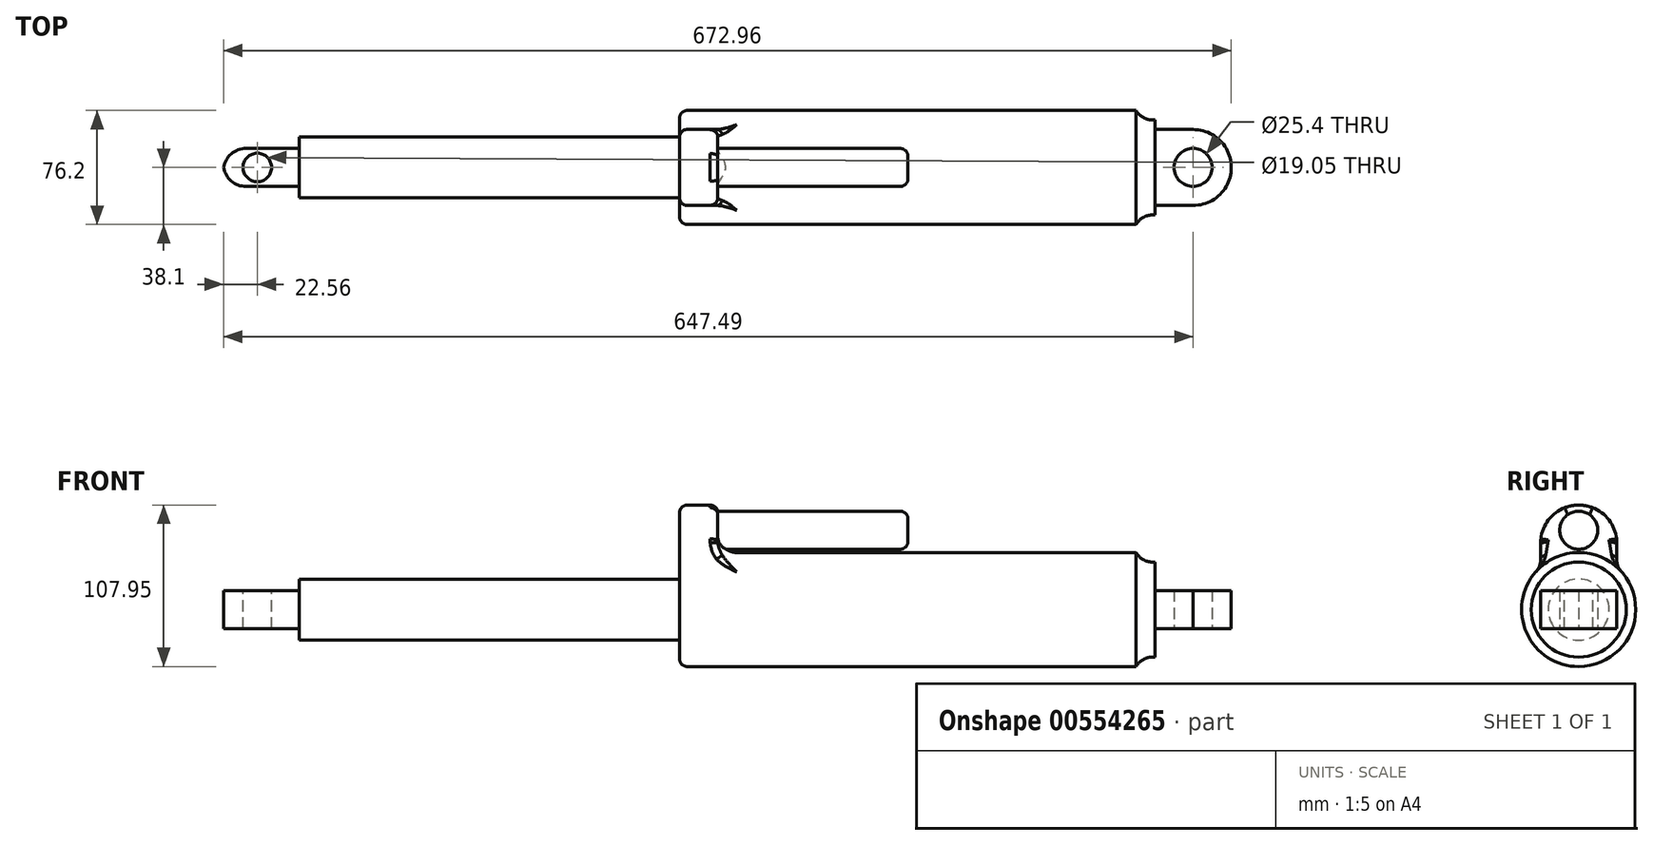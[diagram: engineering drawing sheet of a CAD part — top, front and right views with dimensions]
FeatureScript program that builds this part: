
annotation { "Feature Type Name" : "Feature", "Feature Type Description" : "" }
export const myFeature = defineFeature(function(context is Context, id is Id, definition is map)
    precondition{}
    {
        {
            var Q0;
            Q0=qCreatedBy(makeId("Right.planeOp"),FACE);
            var sketch = newSketch(context, id + "F0", { "sketchPlane" : qUnion([Q0])});
            skCircle(sketch, "E0", {"center": v(0, 0) * mm, "radius": 38.1 * mm});
            skSolve(sketch);
        }
        {
            var Q0;
            Q0=sQuery(id+"F0.wireOp",EDGE,"E0");
            extrude(context, id + "F1", {"bodyType" : ToolBodyType.SURFACE, "surfaceEntities" : qUnion([Q0]), "depth" : 304.8 * mm, "offsetDistance" : 25.4 * mm});
        }
        {
            var Q0;
            Q0=qCreatedBy(makeId("Right.planeOp"),FACE);
            var sketch = newSketch(context, id + "F2", { "sketchPlane" : qUnion([Q0])});
            skCircle(sketch, "E1", {"center": v(0, 0) * mm, "radius": 20.37 * mm});
            skSolve(sketch);
        }
        {
            var Q0;
            Q0=sQuery(id+"F2.wireOp",EDGE,"E1");
            extrude(context, id + "F3", {"bodyType" : ToolBodyType.SURFACE, "surfaceEntities" : qUnion([Q0]), "oppositeDirection" : true, "depth" : 254 * mm, "offsetDistance" : 25.4 * mm});
        }
        {
            var Q0;
            Q0=qCreatedBy(makeId("Right.planeOp"),FACE);
            var sketch = newSketch(context, id + "F4", { "sketchPlane" : qUnion([Q0])});
            skLineSegment(sketch, "E2.bottom", {"start": v(0, 0) * mm, "end": v(25.4, 0) * mm});
            skLineSegment(sketch, "E2.top", {"start": v(0, 69.85) * mm, "end": v(25.4, 69.85) * mm});
            skLineSegment(sketch, "E2.left", {"start": v(0, 0) * mm, "end": v(0, 69.85) * mm});
            skLineSegment(sketch, "E2.right", {"start": v(25.4, 0) * mm, "end": v(25.4, 69.85) * mm});
            skLineSegment(sketch, "E3.bottom", {"start": v(0, 0) * mm, "end": v(-25.4, 0) * mm});
            skLineSegment(sketch, "E3.top", {"start": v(0, 69.85) * mm, "end": v(-25.4, 69.85) * mm});
            skLineSegment(sketch, "E3.right", {"start": v(-25.4, 0) * mm, "end": v(-25.4, 69.85) * mm});
            skSolve(sketch);
        }
        {
            var Q0;
            Q0=makeQuery(id+"F4.imprint","IMPRINT",FACE,{"disambiguationData":[TD([[makeQuery(id+"F4.imprint","IMPRINT",EDGE,{"derivedFrom":sQuery(id+"F4.wireOp",EDGE,"E3.bottom")}),-1.0]])]});
            var Q1;
            Q1=makeQuery(id+"F4.imprint","IMPRINT",FACE,{"disambiguationData":[TD([[makeQuery(id+"F4.imprint","IMPRINT",EDGE,{"derivedFrom":sQuery(id+"F4.wireOp",EDGE,"E2.bottom")}),1.0]])]});
            extrude(context, id + "F5", {"entities" : qUnion([Q0, Q1]), "depth" : 25.4 * mm, "offsetDistance" : 25.4 * mm});
        }
        {
            var Q0;
            Q0=makeQuery(id+"F5.opExtrude","CAP_FACE",FACE,{"disambiguationData":[OSD([sQuery(id+"F4.wireOp",EDGE,"E2.bottom"),sQuery(id+"F4.wireOp",EDGE,"E2.top"),sQuery(id+"F4.wireOp",EDGE,"E2.right"),sQuery(id+"F4.wireOp",EDGE,"E3.bottom"),sQuery(id+"F4.wireOp",EDGE,"E3.top"),sQuery(id+"F4.wireOp",EDGE,"E3.right")])],"isStart":false});
            var sketch = newSketch(context, id + "F6", { "sketchPlane" : qUnion([Q0])});
            skPoint(sketch, "E4", {"position": v(0, 53.06) * mm});
            skCircle(sketch, "E5", {"center": v(0, 53.06) * mm, "radius": 12.7 * mm});
            skSolve(sketch);
        }
        {
            var Q0;
            {var subQ0=sQuery(id+"F6.wireOp",EDGE,"E5");var subQ1=makeQuery(id+"F5.opExtrude","CAP_EDGE",EDGE,{"disambiguationData":[OSD([sQuery(id+"F4.wireOp",EDGE,"E2.top"),sQuery(id+"F4.wireOp",EDGE,"E3.top")])],"isStart":false});var subQ2=makeQuery(id+"F6.imprint","INTERSECT",VERTEX,{"disambiguationData":[OD(0.0)],"derivedFrom":[subQ1,subQ0]});Q0=makeQuery(id+"F6.imprint","IMPRINT",FACE,{"disambiguationData":[TD([[makeQuery(id+"F6.imprint","IMPRINT",EDGE,{"disambiguationData":[TD([[subQ2,1.0]])],"derivedFrom":subQ0}),1.0]])]});}
            extrude(context, id + "F7", {"entities" : qUnion([Q0]), "operationType" : NewBodyOperationType.ADD, "depth" : 127 * mm, "offsetDistance" : 25.4 * mm});
        }
        {
            var Q0;
            Q0=qCreatedBy(makeId("Right.planeOp"),FACE);
            var sketch = newSketch(context, id + "F8", { "sketchPlane" : qUnion([Q0])});
            skLineSegment(sketch, "E6.bottom", {"start": v(25.4, -12.7) * mm, "end": v(-25.4, -12.7) * mm});
            skLineSegment(sketch, "E6.top", {"start": v(25.4, 12.7) * mm, "end": v(-25.4, 12.7) * mm});
            skLineSegment(sketch, "E6.left", {"start": v(25.4, -12.7) * mm, "end": v(25.4, 12.7) * mm});
            skLineSegment(sketch, "E6.right", {"start": v(-25.4, -12.7) * mm, "end": v(-25.4, 12.7) * mm});
            skPoint(sketch, "E6.middle", {"position": v(0, 0) * mm});
            skSolve(sketch);
        }
        {
            var Q0;
            Q0=makeQuery(id+"F8.imprint","IMPRINT",FACE,{"disambiguationData":[TD([[makeQuery(id+"F8.imprint","IMPRINT",EDGE,{"derivedFrom":sQuery(id+"F8.wireOp",EDGE,"E6.bottom")}),-1.0]])]});
            extrude(context, id + "F9", {"entities" : qUnion([Q0]), "operationType" : NewBodyOperationType.ADD, "depth" : 342.9 * mm, "offsetDistance" : 25.4 * mm});
        }
        {
            var Q0;
            Q0=qCreatedBy(makeId("Top.planeOp"),FACE);
            var sketch = newSketch(context, id + "F10", { "sketchPlane" : qUnion([Q0])});
            skPoint(sketch, "E7", {"position": v(343.01, 0) * mm});
            skCircle(sketch, "E8", {"center": v(343.01, 0) * mm, "radius": 25.36 * mm});
            skSolve(sketch);
        }
        {
            var Q0;
            Q0=makeQuery(id+"F10.imprint","IMPRINT",FACE,{"disambiguationData":[TD([[makeQuery(id+"F10.imprint","IMPRINT",EDGE,{"derivedFrom":sQuery(id+"F10.wireOp",EDGE,"E8")}),1.0]])]});
            extrude(context, id + "F11", {"entities" : qUnion([Q0]), "operationType" : NewBodyOperationType.ADD, "depth" : 12.7 * mm, "offsetDistance" : 25.4 * mm});
        }
        {
            var Q0;
            Q0=makeQuery(id+"F11.opExtrude","CAP_FACE",FACE,{"disambiguationData":[OSD([sQuery(id+"F10.wireOp",EDGE,"E8")])],"isStart":true});
            extrude(context, id + "F12", {"entities" : qUnion([Q0]), "operationType" : NewBodyOperationType.ADD, "depth" : 12.7 * mm, "offsetDistance" : 25.4 * mm});
        }
        {
            var Q0;
            Q0=makeQuery(id+"F12.boolean.opBoolean","MERGE",FACE,{"derivedFrom":[makeQuery(id+"F9.opExtrude","SWEPT_FACE",FACE,{"disambiguationData":[OSD([sQuery(id+"F8.wireOp",EDGE,"E6.bottom")])]}),makeQuery(id+"F12.opExtrude","CAP_FACE",FACE,{"disambiguationData":[OSD([sQuery(id+"F10.wireOp",EDGE,"E8")])],"isStart":false})]});
            var sketch = newSketch(context, id + "F13", { "sketchPlane" : qUnion([Q0])});
            skPoint(sketch, "E9", {"position": v(342.9, 0) * mm});
            skSolve(sketch);
        }
        {
            var Q0;
            Q0=sQuery(id+"F13.wireOp",VERTEX,"E9");
            var Q1;
            Q1=makeQuery(id+"F5.opExtrude","SWEPT_BODY",BODY,{"disambiguationData":[OSD([sQuery(id+"F4.wireOp",EDGE,"E2.bottom"),sQuery(id+"F4.wireOp",EDGE,"E2.top"),sQuery(id+"F4.wireOp",EDGE,"E2.right"),sQuery(id+"F4.wireOp",EDGE,"E3.bottom"),sQuery(id+"F4.wireOp",EDGE,"E3.top"),sQuery(id+"F4.wireOp",EDGE,"E3.right")])]});
            hole(context, id + "F14", {"style" : HoleStyle.SIMPLE, "endStyle" : HoleEndStyle.THROUGH, "holeDiameter" : 25.4 * mm, "isTappedThrough" : true, "tappedDepth" : 12.7 * mm, "tapClearance" : 3, "locations" : qUnion([Q0]), "scope" : qUnion([Q1])});
        }
        {
            var Q0;
            Q0=qCreatedBy(makeId("Right.planeOp"),FACE);
            var sketch = newSketch(context, id + "F15", { "sketchPlane" : qUnion([Q0])});
            skLineSegment(sketch, "E10.bottom", {"start": v(7.2, -12.7) * mm, "end": v(-7.2, -12.7) * mm});
            skLineSegment(sketch, "E10.top", {"start": v(7.2, 12.7) * mm, "end": v(-7.2, 12.7) * mm});
            skLineSegment(sketch, "E10.left", {"start": v(7.2, -12.7) * mm, "end": v(7.2, 12.7) * mm});
            skLineSegment(sketch, "E10.right", {"start": v(-7.2, -12.7) * mm, "end": v(-7.2, 12.7) * mm});
            skPoint(sketch, "E10.middle", {"position": v(0, 0) * mm});
            skSolve(sketch);
        }
        {
            var Q0;
            Q0=makeQuery(id+"F15.imprint","IMPRINT",FACE,{"disambiguationData":[TD([[makeQuery(id+"F15.imprint","IMPRINT",EDGE,{"derivedFrom":sQuery(id+"F15.wireOp",EDGE,"E10.bottom")}),-1.0]])]});
            extrude(context, id + "F16", {"entities" : qUnion([Q0]), "operationType" : NewBodyOperationType.ADD, "depth" : 25.4 * mm, "offsetDistance" : 25.4 * mm});
        }
        {
            var Q0;
            Q0=qCreatedBy(makeId("Right.planeOp"),FACE);
            var sketch = newSketch(context, id + "F17", { "sketchPlane" : qUnion([Q0])});
            skLineSegment(sketch, "E11.bottom", {"start": v(-12.7, -12.7) * mm, "end": v(12.7, -12.7) * mm});
            skLineSegment(sketch, "E11.top", {"start": v(-12.7, 12.7) * mm, "end": v(12.7, 12.7) * mm});
            skLineSegment(sketch, "E11.left", {"start": v(-12.7, -12.7) * mm, "end": v(-12.7, 12.7) * mm});
            skLineSegment(sketch, "E11.right", {"start": v(12.7, -12.7) * mm, "end": v(12.7, 12.7) * mm});
            skPoint(sketch, "E11.middle", {"position": v(0, 0) * mm});
            skSolve(sketch);
        }
        {
            var Q0;
            Q0=makeQuery(id+"F17.imprint","IMPRINT",FACE,{"disambiguationData":[TD([[makeQuery(id+"F17.imprint","IMPRINT",EDGE,{"derivedFrom":sQuery(id+"F17.wireOp",EDGE,"E11.bottom")}),1.0]])]});
            extrude(context, id + "F18", {"entities" : qUnion([Q0]), "operationType" : NewBodyOperationType.ADD, "oppositeDirection" : true, "depth" : 304.8 * mm, "offsetDistance" : 25.4 * mm});
        }
        {
            var Q0;
            Q0=makeQuery(id+"F18.opExtrude","CAP_EDGE",EDGE,{"disambiguationData":[OSD([sQuery(id+"F17.wireOp",EDGE,"E11.right")])],"isStart":false});
            var Q1;
            Q1=makeQuery(id+"F18.opExtrude","CAP_EDGE",EDGE,{"disambiguationData":[OSD([sQuery(id+"F17.wireOp",EDGE,"E11.left")])],"isStart":false});
            fillet(context, id + "F19", {"entities" : qUnion([Q0, Q1]), "radius" : 15.24 * mm, "tangentPropagation" : true, "allowEdgeOverflow" : false});
        }
        {
            var Q0;
            Q0=makeQuery(id+"F18.opExtrude","SWEPT_FACE",FACE,{"disambiguationData":[OSD([sQuery(id+"F17.wireOp",EDGE,"E11.top")])]});
            var sketch = newSketch(context, id + "F20", { "sketchPlane" : qUnion([Q0])});
            skPoint(sketch, "E12", {"position": v(-282.03, 0) * mm});
            skSolve(sketch);
        }
        {
            var Q0;
            Q0=sQuery(id+"F20.wireOp",VERTEX,"E12");
            var Q1;
            Q1=makeQuery(id+"F5.opExtrude","SWEPT_BODY",BODY,{"disambiguationData":[OSD([sQuery(id+"F4.wireOp",EDGE,"E2.bottom"),sQuery(id+"F4.wireOp",EDGE,"E2.top"),sQuery(id+"F4.wireOp",EDGE,"E2.right"),sQuery(id+"F4.wireOp",EDGE,"E3.bottom"),sQuery(id+"F4.wireOp",EDGE,"E3.top"),sQuery(id+"F4.wireOp",EDGE,"E3.right")])]});
            hole(context, id + "F21", {"style" : HoleStyle.SIMPLE, "endStyle" : HoleEndStyle.THROUGH, "holeDiameter" : 19.05 * mm, "isTappedThrough" : true, "tappedDepth" : 12.7 * mm, "tapClearance" : 3, "locations" : qUnion([Q0]), "scope" : qUnion([Q1])});
        }
        {
            var Q0;
            Q0=makeQuery(id+"F5.opExtrude","SWEPT_EDGE",EDGE,{"disambiguationData":[OSD([sQuery(id+"F4.wireOp",EDGE,"E3.top"),sQuery(id+"F4.wireOp",EDGE,"E3.right")])]});
            var Q1;
            Q1=makeQuery(id+"F5.opExtrude","SWEPT_EDGE",EDGE,{"disambiguationData":[OSD([sQuery(id+"F4.wireOp",EDGE,"E2.top"),sQuery(id+"F4.wireOp",EDGE,"E2.right")])]});
            fillet(context, id + "F22", {"entities" : qUnion([Q0, Q1]), "radius" : 25.4 * mm, "tangentPropagation" : true, "allowEdgeOverflow" : false});
        }
        {
            var Q0;
            Q0=makeQuery(id+"F7.opExtrude","CAP_EDGE",EDGE,{"disambiguationData":[OSD([sQuery(id+"F6.wireOp",EDGE,"E5")])],"isStart":false});
            fillet(context, id + "F23", {"entities" : qUnion([Q0]), "radius" : 5.08 * mm, "tangentPropagation" : true, "allowEdgeOverflow" : false});
        }
        {
            var Q0;
            Q0=qCreatedBy(makeId("Right.planeOp"),FACE);
            var sketch = newSketch(context, id + "F24", { "sketchPlane" : qUnion([Q0])});
            skCircle(sketch, "E13", {"center": v(0, 0) * mm, "radius": 31.75 * mm});
            skSolve(sketch);
        }
        {
            var Q0;
            Q0=sQuery(id+"F24.wireOp",EDGE,"E13");
            extrude(context, id + "F25", {"bodyType" : ToolBodyType.SURFACE, "surfaceEntities" : qUnion([Q0]), "depth" : 317.5 * mm, "offsetDistance" : 25.4 * mm});
        }
        {
            var Q0;
            Q0 = qSketchRegion(id + "F0", true);
            extrude(context, id + "F26", {"entities" : qUnion([Q0]), "operationType" : NewBodyOperationType.ADD, "depth" : 304.8 * mm, "offsetDistance" : 25.4 * mm});
        }
        {
            var Q0;
            Q0 = qSketchRegion(id + "F24", true);
            extrude(context, id + "F27", {"entities" : qUnion([Q0]), "operationType" : NewBodyOperationType.ADD, "depth" : 317.5 * mm, "offsetDistance" : 25.4 * mm});
        }
        {
            var Q0;
            Q0 = qSketchRegion(id + "F2", true);
            extrude(context, id + "F28", {"entities" : qUnion([Q0]), "operationType" : NewBodyOperationType.ADD, "oppositeDirection" : true, "depth" : 254 * mm, "offsetDistance" : 25.4 * mm});
        }
        {
            var Q0;
            Q0=makeQuery(id+"F27.boolean.opBoolean","INTERSECT",EDGE,{"derivedFrom":[makeQuery(id+"F26.opExtrude","CAP_FACE",FACE,{"disambiguationData":[OSD([sQuery(id+"F0.wireOp",EDGE,"E0")])],"isStart":false}),makeQuery(id+"F27.opExtrude","SWEPT_FACE",FACE,{"disambiguationData":[OSD([sQuery(id+"F24.wireOp",EDGE,"E13")])]})]});
            fillet(context, id + "F29", {"entities" : qUnion([Q0]), "radius" : 12.7 * mm, "tangentPropagation" : true, "allowEdgeOverflow" : false});
        }
        {
            var Q0;
            Q0=makeQuery(id+"F26.boolean.opBoolean","INTERSECT",EDGE,{"derivedFrom":[makeQuery(id+"F5.opExtrude","CAP_FACE",FACE,{"disambiguationData":[OSD([sQuery(id+"F4.wireOp",EDGE,"E2.bottom"),sQuery(id+"F4.wireOp",EDGE,"E2.top"),sQuery(id+"F4.wireOp",EDGE,"E2.right"),sQuery(id+"F4.wireOp",EDGE,"E3.bottom"),sQuery(id+"F4.wireOp",EDGE,"E3.top"),sQuery(id+"F4.wireOp",EDGE,"E3.right")])],"isStart":false}),makeQuery(id+"F26.opExtrude","SWEPT_FACE",FACE,{"disambiguationData":[OSD([sQuery(id+"F0.wireOp",EDGE,"E0")])]})]});
            fillet(context, id + "F30", {"entities" : qUnion([Q0]), "radius" : 12.7 * mm, "tangentPropagation" : true, "allowEdgeOverflow" : false});
        }
        {
            var Q0;
            Q0=makeQuery(id+"F26.boolean.opBoolean","INTERSECT",EDGE,{"derivedFrom":[makeQuery(id+"F9.boolean.opBoolean","MERGE",FACE,{"derivedFrom":[makeQuery(id+"F5.opExtrude","SWEPT_FACE",FACE,{"disambiguationData":[OSD([sQuery(id+"F4.wireOp",EDGE,"E3.right")])]}),makeQuery(id+"F9.opExtrude","SWEPT_FACE",FACE,{"disambiguationData":[OSD([sQuery(id+"F8.wireOp",EDGE,"E6.right")])]})]}),makeQuery(id+"F26.opExtrude","SWEPT_FACE",FACE,{"disambiguationData":[OSD([sQuery(id+"F0.wireOp",EDGE,"E0")])]})]});
            var Q1;
            Q1=makeQuery(id+"F26.boolean.opBoolean","INTERSECT",EDGE,{"derivedFrom":[makeQuery(id+"F9.boolean.opBoolean","MERGE",FACE,{"derivedFrom":[makeQuery(id+"F5.opExtrude","SWEPT_FACE",FACE,{"disambiguationData":[OSD([sQuery(id+"F4.wireOp",EDGE,"E2.right")])]}),makeQuery(id+"F9.opExtrude","SWEPT_FACE",FACE,{"disambiguationData":[OSD([sQuery(id+"F8.wireOp",EDGE,"E6.left")])]})]}),makeQuery(id+"F26.opExtrude","SWEPT_FACE",FACE,{"disambiguationData":[OSD([sQuery(id+"F0.wireOp",EDGE,"E0")])]})]});
            fillet(context, id + "F31", {"entities" : qUnion([Q0, Q1]), "radius" : 12.7 * mm, "tangentPropagation" : true, "allowEdgeOverflow" : false});
        }
        {
            var Q0;
            Q0=makeQuery(id+"F26.opExtrude","CAP_EDGE",EDGE,{"disambiguationData":[OSD([sQuery(id+"F0.wireOp",EDGE,"E0")])],"isStart":true});
            fillet(context, id + "F32", {"entities" : qUnion([Q0]), "radius" : 5.08 * mm, "tangentPropagation" : true, "allowEdgeOverflow" : false});
        }
        {
            var Q0;
            {var subQ0=sQuery(id+"F4.wireOp",EDGE,"E2.right");var subQ1=sQuery(id+"F4.wireOp",EDGE,"E2.top");Q0=makeQuery(id+"F22.opFillet","BLEND_EDGE",EDGE,{"blendedFrom":[makeQuery(id+"F5.opExtrude","SWEPT_EDGE",EDGE,{"disambiguationData":[OSD([subQ1,subQ0])]}),makeQuery(id+"F5.opExtrude","CAP_FACE",FACE,{"disambiguationData":[OSD([sQuery(id+"F4.wireOp",EDGE,"E2.bottom"),subQ1,subQ0,sQuery(id+"F4.wireOp",EDGE,"E3.bottom"),sQuery(id+"F4.wireOp",EDGE,"E3.top"),sQuery(id+"F4.wireOp",EDGE,"E3.right")])],"isStart":false})],"blendedInto":[makeQuery(id+"F5.opExtrude","CAP_FACE",FACE,{"disambiguationData":[OSD([sQuery(id+"F4.wireOp",EDGE,"E2.bottom"),subQ1,subQ0,sQuery(id+"F4.wireOp",EDGE,"E3.bottom"),sQuery(id+"F4.wireOp",EDGE,"E3.top"),sQuery(id+"F4.wireOp",EDGE,"E3.right")])],"isStart":false})]});}
            fillet(context, id + "F33", {"entities" : qUnion([Q0]), "radius" : 5.08 * mm, "tangentPropagation" : true, "allowEdgeOverflow" : false});
        }
    });
